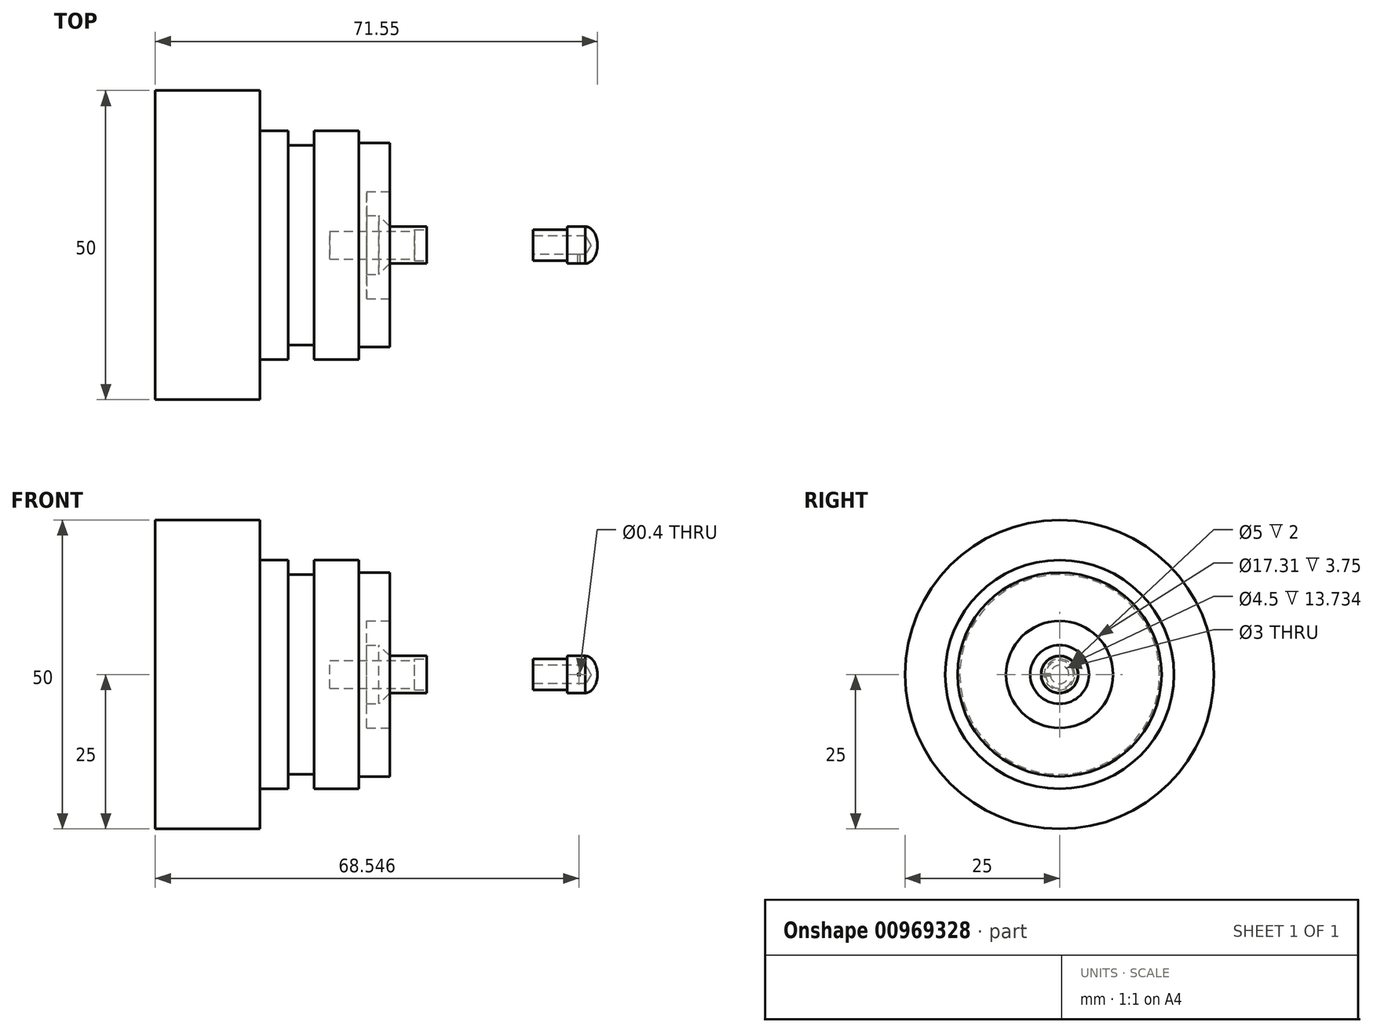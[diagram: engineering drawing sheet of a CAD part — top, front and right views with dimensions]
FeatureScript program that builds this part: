
annotation { "Feature Type Name" : "Feature", "Feature Type Description" : "" }
export const myFeature = defineFeature(function(context is Context, id is Id, definition is map)
    precondition{}
    {
        {
            var Q0;
            Q0=qCreatedBy(makeId("Front.planeOp"),FACE);
            var sketch = newSketch(context, id + "F0", { "sketchPlane" : qUnion([Q0])});
            skLineSegment(sketch, "E0", {"start": v(0, 0) * mm, "end": v(21.32, 0) * mm, "construction": true});
            skLineSegment(sketch, "E1", {"start": v(3.55, 2.5) * mm, "end": v(3.55, 1.5) * mm});
            skLineSegment(sketch, "E2", {"start": v(3.55, 1.5) * mm, "end": v(12.07, 1.5) * mm});
            skLineSegment(sketch, "E3", {"start": v(12.07, 1.5) * mm, "end": v(12.98, 0) * mm});
            skLineSegment(sketch, "E4", {"start": v(12.98, 0) * mm, "end": v(13.98, 0) * mm});
            skEllipticalArc(sketch, "E5", {});
            skLineSegment(sketch, "E6", {"start": v(3.55, 2.5) * mm, "end": v(9.08, 2.5) * mm});
            skLineSegment(sketch, "E7", {"start": v(9.08, 3) * mm, "end": v(9.08, 2.5) * mm});
            skLineSegment(sketch, "E8", {"start": v(9.08, 3) * mm, "end": v(11.98, 3) * mm});
            const initialGuessF0  = {"E5": [0.011976268827915191, 0, 0, 1, 0.003, 0.002, 4.71238898038469, 0]};
            skSetInitialGuess(sketch, initialGuessF0);
            skSolve(sketch);
        }
        {
            var Q0;
            Q0 = qSketchRegion(id + "F0", true);
            var Q1;
            Q1=sQuery(id+"F0.wireOp",EDGE,"E0");
            revolve(context, id + "F1", {"surfaceOperationType" : NewSurfaceOperationType.NEW, "entities" : qUnion([Q0]), "axis" : qUnion([Q1]), "revolveType" : RevolveType.FULL});
        }
        {
            var Q0;
            Q0=qCreatedBy(makeId("Front.planeOp"),FACE);
            var sketch = newSketch(context, id + "F2", { "sketchPlane" : qUnion([Q0])});
            skCircle(sketch, "E9", {"center": v(10.98, 0) * mm, "radius": 0.2 * mm});
            skSolve(sketch);
        }
        {
            var Q0;
            Q0 = qSketchRegion(id + "F2", true);
            extrude(context, id + "F3", {"entities" : qUnion([Q0]), "operationType" : NewBodyOperationType.REMOVE, "depth" : 25 * mm, "offsetDistance" : 25 * mm});
        }
        {
            var Q0;
            Q0=qCreatedBy(makeId("Front.planeOp"),FACE);
            var sketch = newSketch(context, id + "F4", { "sketchPlane" : qUnion([Q0])});
            skLineSegment(sketch, "E10", {"start": v(-13.62, 2.5) * mm, "end": v(-13.62, 3) * mm});
            skLineSegment(sketch, "E11", {"start": v(-13.62, 3) * mm, "end": v(-19.62, 3) * mm});
            skLineSegment(sketch, "E12", {"start": v(-23.37, 4.75) * mm, "end": v(-23.37, 8.66) * mm});
            skLineSegment(sketch, "E13", {"start": v(-23.37, 8.66) * mm, "end": v(-19.62, 8.66) * mm});
            skLineSegment(sketch, "E14", {"start": v(-19.62, 8.66) * mm, "end": v(-19.62, 16.5) * mm});
            skLineSegment(sketch, "E15", {"start": v(-19.62, 16.5) * mm, "end": v(-24.62, 16.5) * mm});
            skLineSegment(sketch, "E16", {"start": v(-24.62, 16.5) * mm, "end": v(-24.62, 18.5) * mm});
            skLineSegment(sketch, "E17", {"start": v(-24.62, 18.5) * mm, "end": v(-31.89, 18.5) * mm});
            skLineSegment(sketch, "E18", {"start": v(-31.89, 18.5) * mm, "end": v(-31.89, 16.15) * mm});
            skLineSegment(sketch, "E19", {"start": v(-31.89, 16.15) * mm, "end": v(-36.09, 16.15) * mm});
            skLineSegment(sketch, "E20", {"start": v(-36.09, 16.15) * mm, "end": v(-36.09, 18.5) * mm});
            skLineSegment(sketch, "E21", {"start": v(-36.09, 18.5) * mm, "end": v(-40.61, 18.5) * mm});
            skLineSegment(sketch, "E22", {"start": v(-57.57, 0) * mm, "end": v(-29.36, 0) * mm});
            skLineSegment(sketch, "E23", {"start": v(-29.36, 0) * mm, "end": v(-29.36, 2.25) * mm});
            skLineSegment(sketch, "E24", {"start": v(0, 0) * mm, "end": v(-85.36, 0) * mm, "construction": true});
            skLineSegment(sketch, "E25", {"start": v(-13.62, 2.5) * mm, "end": v(-15.62, 2.5) * mm});
            skLineSegment(sketch, "E26", {"start": v(-15.62, 2.5) * mm, "end": v(-15.62, 2.25) * mm});
            skLineSegment(sketch, "E27", {"start": v(-15.62, 2.25) * mm, "end": v(-29.36, 2.25) * mm});
            skLineSegment(sketch, "E28", {"start": v(-19.62, 3) * mm, "end": v(-21.37, 4.75) * mm});
            skLineSegment(sketch, "E29", {"start": v(-21.37, 4.75) * mm, "end": v(-23.37, 4.75) * mm});
            skLineSegment(sketch, "E30", {"start": v(-40.61, 18.5) * mm, "end": v(-40.61, 25) * mm});
            skLineSegment(sketch, "E31", {"start": v(-40.61, 25) * mm, "end": v(-57.57, 25) * mm});
            skLineSegment(sketch, "E32", {"start": v(-57.57, 25) * mm, "end": v(-57.57, 0) * mm});
            skSolve(sketch);
        }
        {
            var Q0;
            Q0 = qSketchRegion(id + "F4", true);
            var Q1;
            Q1=sQuery(id+"F4.wireOp",EDGE,"E24");
            revolve(context, id + "F5", {"surfaceOperationType" : NewSurfaceOperationType.NEW, "entities" : qUnion([Q0]), "axis" : qUnion([Q1]), "revolveType" : RevolveType.FULL});
        }
    });
